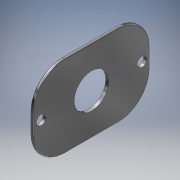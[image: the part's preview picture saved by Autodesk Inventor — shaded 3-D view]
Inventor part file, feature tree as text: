
AUTODESK INVENTOR PART (.ipt)
format: ipt  version: 2018 (Build 220112000, 112)  size: 155,648 bytes
history: native  units: mm
features: extrude x1, fillet x1, sketch x1
ambient origin geometry x8: Origin, YZ Plane, XZ Plane, XY Plane, X Axis, Y Axis, Z Axis, Center Point
bodies: Solid1 (feature_tree)
feature tree (3):
  extrude  "Extrusion1"  Depth=0.25mm
  fillet  "Fillet1"  Radius=37.0mm
  sketch  "Sketch1"  dims[d0=11.0mm d1=2.5mm d2=37.0mm d3=26.0mm d4=3.1mm d5=10.0mm d6=1.0mm d7=0.0mm d8=0.25mm]
